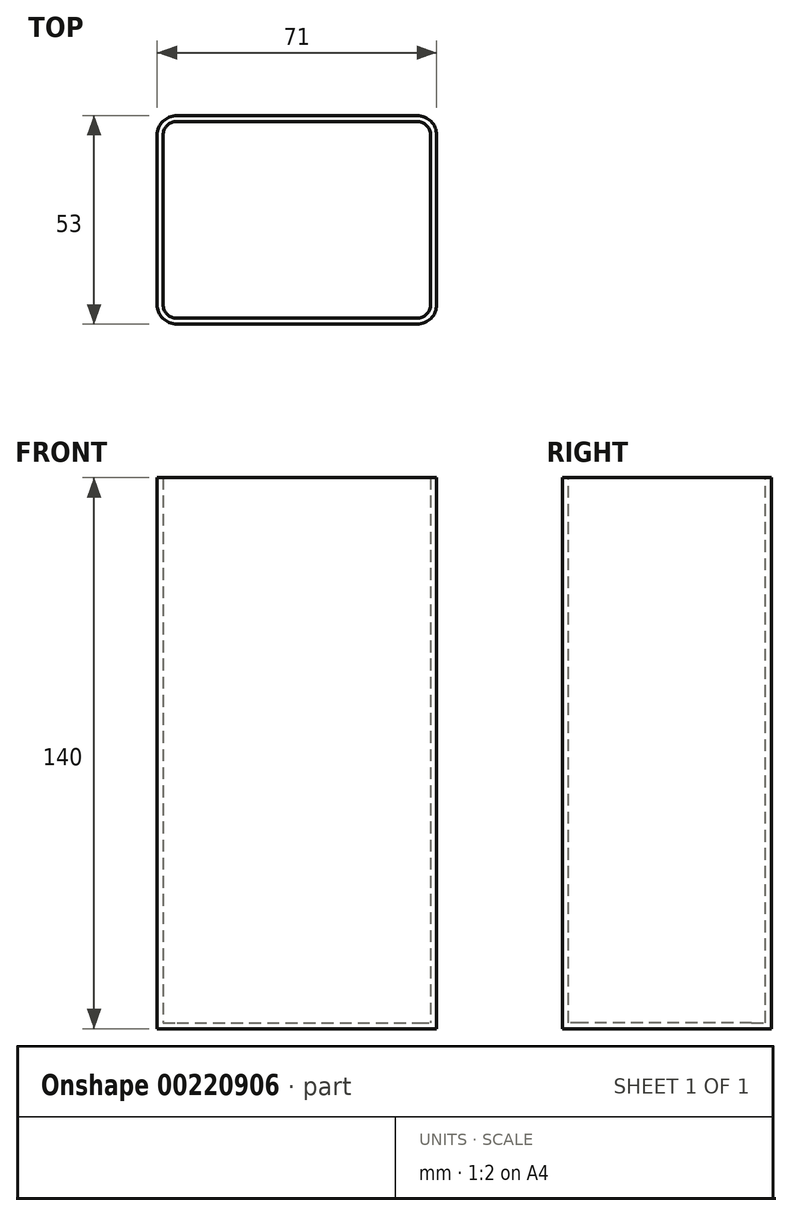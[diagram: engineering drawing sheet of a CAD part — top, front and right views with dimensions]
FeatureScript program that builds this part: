
annotation { "Feature Type Name" : "Feature", "Feature Type Description" : "" }
export const myFeature = defineFeature(function(context is Context, id is Id, definition is map)
    precondition{}
    {
        {
            var Q0;
            Q0=qCreatedBy(makeId("Top.planeOp"),FACE);
            var sketch = newSketch(context, id + "F0", { "sketchPlane" : qUnion([Q0])});
            skLineSegment(sketch, "E0.bottom", {"start": v(-35.5, 26.5) * mm, "end": v(35.5, 26.5) * mm});
            skLineSegment(sketch, "E0.top", {"start": v(-35.5, -26.5) * mm, "end": v(35.5, -26.5) * mm});
            skLineSegment(sketch, "E0.left", {"start": v(-35.5, 26.5) * mm, "end": v(-35.5, -26.5) * mm});
            skLineSegment(sketch, "E0.right", {"start": v(35.5, 26.5) * mm, "end": v(35.5, -26.5) * mm});
            skPoint(sketch, "E0.middle", {"position": v(0, 0) * mm});
            skSolve(sketch);
        }
        {
            var Q0;
            Q0 = qSketchRegion(id + "F0", true);
            extrude(context, id + "F1", {"entities" : qUnion([Q0]), "depth" : 140 * mm});
        }
        {
            var Q0;
            Q0=makeQuery(id+"F1.opExtrude","SWEPT_EDGE",EDGE,{"disambiguationData":[OSD([sQuery(id+"F0.wireOp",EDGE,"E0.bottom"),sQuery(id+"F0.wireOp",EDGE,"E0.right")])]});
            var Q1;
            Q1=makeQuery(id+"F1.opExtrude","SWEPT_EDGE",EDGE,{"disambiguationData":[OSD([sQuery(id+"F0.wireOp",EDGE,"E0.top"),sQuery(id+"F0.wireOp",EDGE,"E0.right")])]});
            var Q2;
            Q2=makeQuery(id+"F1.opExtrude","SWEPT_EDGE",EDGE,{"disambiguationData":[OSD([sQuery(id+"F0.wireOp",EDGE,"E0.top"),sQuery(id+"F0.wireOp",EDGE,"E0.left")])]});
            var Q3;
            Q3=makeQuery(id+"F1.opExtrude","SWEPT_EDGE",EDGE,{"disambiguationData":[OSD([sQuery(id+"F0.wireOp",EDGE,"E0.bottom"),sQuery(id+"F0.wireOp",EDGE,"E0.left")])]});
            fillet(context, id + "F2", {"entities" : qUnion([Q0, Q1, Q2, Q3]), "radius" : 5 * mm, "tangentPropagation" : true, "allowEdgeOverflow" : false});
        }
        {
            var Q0;
            Q0=makeQuery(id+"F1.opExtrude","CAP_FACE",FACE,{"disambiguationData":[OSD([sQuery(id+"F0.wireOp",EDGE,"E0.bottom"),sQuery(id+"F0.wireOp",EDGE,"E0.top"),sQuery(id+"F0.wireOp",EDGE,"E0.left"),sQuery(id+"F0.wireOp",EDGE,"E0.right")])],"isStart":false});
            shell(context, id + "F3", {"entities" : qUnion([Q0]), "thickness" : 1.5 * mm});
        }
    });
